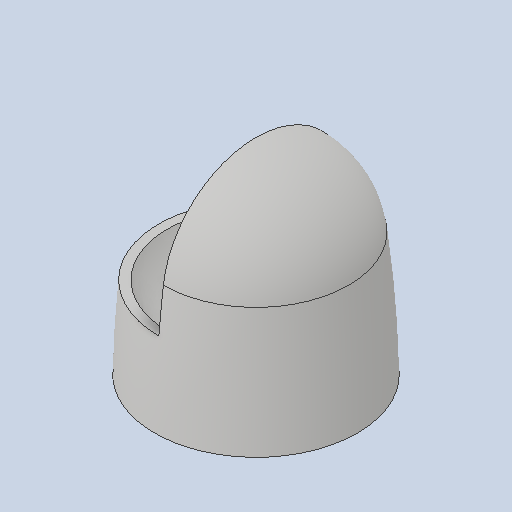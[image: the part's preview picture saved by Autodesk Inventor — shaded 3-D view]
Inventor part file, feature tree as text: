
AUTODESK INVENTOR PART (.ipt)
format: ipt  version: 2025 (Build 290162010, 162A)  size: 143,360 bytes
history: native  units: mm
features: sketch x3, revolve x2, other x1, extrude x1
ambient origin geometry x8: Origin, YZ Plane, XZ Plane, XY Plane, X Axis, Y Axis, Z Axis, Center Point
bodies: Body1 (feature_tree)
feature tree (7):
  other  "Твердое тело1"
  revolve  "Вращение1"
  revolve  "Вращение2"
  extrude  "Выдавливание1"  Depth=100.0mm
  sketch  "Эскиз1"
  sketch  "Эскиз2"
  sketch  "Эскиз3"
